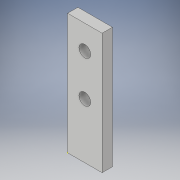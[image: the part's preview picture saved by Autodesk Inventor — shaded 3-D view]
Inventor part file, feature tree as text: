
AUTODESK INVENTOR PART (.ipt)
format: ipt  version: 2017 (Build 210142000, 142)  size: 104,448 bytes
history: native  units: in
note: dims shown in document units (in); Inventor stores cm internally (conversion verified against a paired STEP export)
features: sketch x3, extrude x1, hole x1
ambient origin geometry x8: Origin, YZ Plane, XZ Plane, XY Plane, X Axis, Y Axis, Z Axis, Center Point
bodies: Solid1 (feature_tree)
feature tree (5):
  extrude  "Extrusion1"  Depth=1.378in
  hole  "Hole1"  [1 undecoded]
  sketch  "Sketch3"  dims[d5=0.1969in d6=0.4724in d7=0.1969in d8=0.1339in d9=0.2362in d10=0.1575in d11=0.0787in d12=90.0deg d13=0.315in d14=0.8108in]
  sketch  "Sketch1"  dims[d0=0.3937in d1=1.378in]
  sketch  "Sketch2"  dims[d2=0.1181in d3=0.0in d4=0.2756in]
note: 1 required parameter value undecoded (feature->parameter linkage not recoverable at this tier; creation-order binding heuristic only, values carry confidence <= 0.55)
